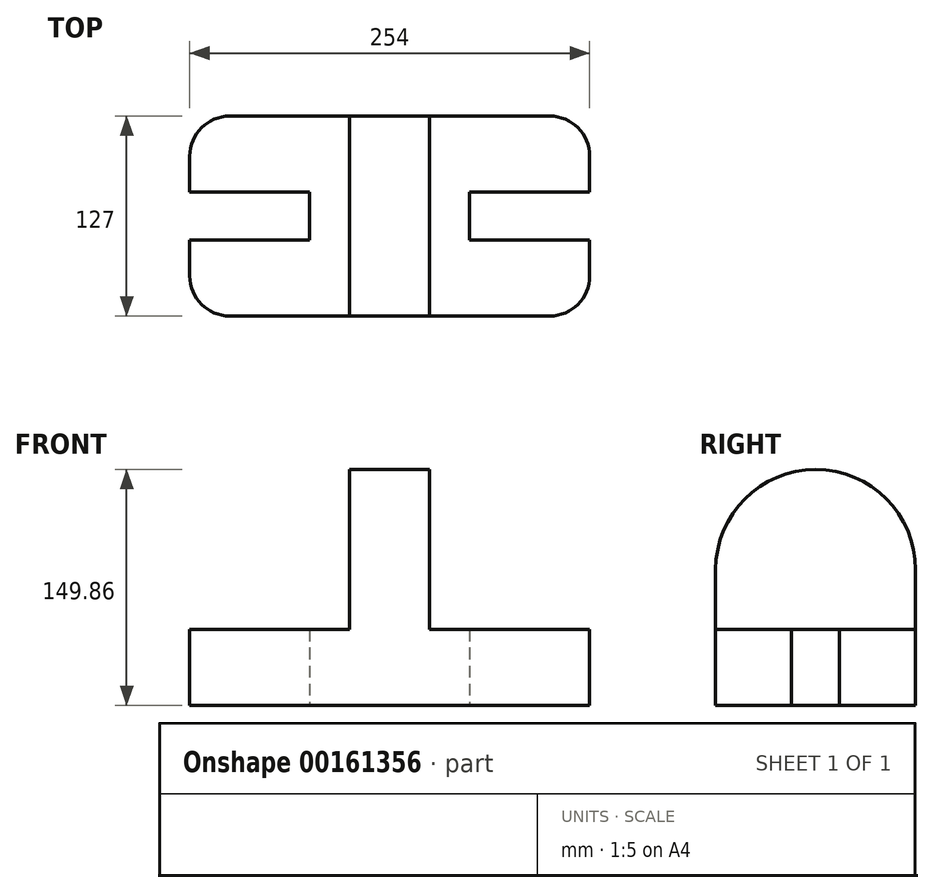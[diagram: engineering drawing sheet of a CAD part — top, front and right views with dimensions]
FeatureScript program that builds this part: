
annotation { "Feature Type Name" : "Feature", "Feature Type Description" : "" }
export const myFeature = defineFeature(function(context is Context, id is Id, definition is map)
    precondition{}
    {
        {
            var Q0;
            Q0=qCreatedBy(makeId("Top.planeOp"),FACE);
            var sketch = newSketch(context, id + "F0", { "sketchPlane" : qUnion([Q0])});
            skLineSegment(sketch, "E0", {"start": v(0, 0) * mm, "end": v(0, 48.26) * mm});
            skLineSegment(sketch, "E1", {"start": v(0, 48.26) * mm, "end": v(-76.2, 48.26) * mm});
            skLineSegment(sketch, "E2", {"start": v(-76.2, 48.26) * mm, "end": v(-76.2, 78.74) * mm});
            skLineSegment(sketch, "E3", {"start": v(-76.2, 78.74) * mm, "end": v(0, 78.74) * mm});
            skLineSegment(sketch, "E4", {"start": v(0, 78.74) * mm, "end": v(0, 127) * mm});
            skLineSegment(sketch, "E5", {"start": v(0, 127) * mm, "end": v(-254, 127) * mm});
            skLineSegment(sketch, "E6", {"start": v(0, 0) * mm, "end": v(-254, 0) * mm});
            skLineSegment(sketch, "E7", {"start": v(-254, 127) * mm, "end": v(-254, 78.74) * mm});
            skLineSegment(sketch, "E8", {"start": v(-254, 0) * mm, "end": v(-254, 48.26) * mm});
            skLineSegment(sketch, "E9", {"start": v(-254, 48.26) * mm, "end": v(-177.8, 48.26) * mm});
            skLineSegment(sketch, "E10", {"start": v(-177.8, 48.26) * mm, "end": v(-177.8, 78.74) * mm});
            skLineSegment(sketch, "E11", {"start": v(-177.8, 78.74) * mm, "end": v(-254, 78.74) * mm});
            skLineSegment(sketch, "E12", {"start": v(-152.4, 127) * mm, "end": v(-101.6, 127) * mm});
            skSolve(sketch);
        }
        {
            var Q0;
            {var subQ1=sQuery(id+"F0.wireOp",EDGE,"E7");Q0=makeQuery(id+"F0.imprint","IMPRINT",FACE,{"disambiguationData":[TD([[makeQuery(id+"F0.imprint","IMPRINT",EDGE,{"derivedFrom":subQ1}),1.0]])]});}
            var Q1;
            {var subQ0=sQuery(id+"F0.wireOp",EDGE,"2u5OPpGf-hsZS-RswZ-xJ63-mRApOYJbijJj");Q1=makeQuery(id+"F0.imprint","IMPRINT",FACE,{"disambiguationData":[TD([[makeQuery(id+"F0.imprint","IMPRINT",EDGE,{"derivedFrom":subQ0}),1.0]])]});}
            var Q2;
            {var subQ0=sQuery(id+"F0.wireOp",EDGE,"E0");Q2=makeQuery(id+"F0.imprint","IMPRINT",FACE,{"disambiguationData":[TD([[makeQuery(id+"F0.imprint","IMPRINT",EDGE,{"derivedFrom":subQ0}),1.0]])]});}
            extrude(context, id + "F1", {"entities" : qUnion([Q0, Q1, Q2]), "depth" : 48.26 * mm});
        }
        {
            var Q0;
            Q0=makeQuery(id+"F1.opExtrude","CAP_FACE",FACE,{"disambiguationData":[OSD([sQuery(id+"F0.wireOp",EDGE,"E0"),sQuery(id+"F0.wireOp",EDGE,"E1"),sQuery(id+"F0.wireOp",EDGE,"E2"),sQuery(id+"F0.wireOp",EDGE,"E3"),sQuery(id+"F0.wireOp",EDGE,"E4"),sQuery(id+"F0.wireOp",EDGE,"E5"),sQuery(id+"F0.wireOp",EDGE,"E6"),sQuery(id+"F0.wireOp",EDGE,"E7"),sQuery(id+"F0.wireOp",EDGE,"E8"),sQuery(id+"F0.wireOp",EDGE,"E9"),sQuery(id+"F0.wireOp",EDGE,"E10"),sQuery(id+"F0.wireOp",EDGE,"E11"),sQuery(id+"F0.wireOp",EDGE,"E12")])],"isStart":false});
            var sketch = newSketch(context, id + "F2", { "sketchPlane" : qUnion([Q0])});
            skLineSegment(sketch, "E13", {"start": v(-127, 127) * mm, "end": v(-152.4, 127) * mm});
            skLineSegment(sketch, "E14", {"start": v(-127, 127) * mm, "end": v(-101.6, 127) * mm});
            skLineSegment(sketch, "E15", {"start": v(-152.4, 127) * mm, "end": v(-152.4, 0) * mm});
            skLineSegment(sketch, "E16", {"start": v(-101.6, 127) * mm, "end": v(-101.6, 0) * mm});
            skSolve(sketch);
        }
        {
            var Q0;
            Q0=makeQuery(id+"F2.imprint","IMPRINT",FACE,{"disambiguationData":[TD([[makeQuery(id+"F2.imprint","IMPRINT",EDGE,{"derivedFrom":sQuery(id+"F2.wireOp",EDGE,"E13")}),1.0]])]});
            extrude(context, id + "F3", {"entities" : qUnion([Q0]), "operationType" : NewBodyOperationType.ADD, "depth" : 101.6 * mm});
        }
        {
            var Q0;
            Q0=makeQuery(id+"F3.opExtrude","CAP_EDGE",EDGE,{"disambiguationData":[OSD([sQuery(id+"F0.wireOp",EDGE,"E6")])],"isStart":false});
            var Q1;
            Q1=makeQuery(id+"F3.opExtrude","CAP_EDGE",EDGE,{"disambiguationData":[OSD([sQuery(id+"F2.wireOp",EDGE,"E13"),sQuery(id+"F2.wireOp",EDGE,"E14")])],"isStart":false});
            fillet(context, id + "F4", {"entities" : qUnion([Q0, Q1]), "radius" : 63.5 * mm, "tangentPropagation" : true, "allowEdgeOverflow" : false});
        }
        {
            var Q0;
            Q0=makeQuery(id+"F1.opExtrude","SWEPT_EDGE",EDGE,{"disambiguationData":[OSD([sQuery(id+"F0.wireOp",EDGE,"E6"),sQuery(id+"F0.wireOp",EDGE,"E8")])]});
            var Q1;
            Q1=makeQuery(id+"F1.opExtrude","SWEPT_EDGE",EDGE,{"disambiguationData":[OSD([sQuery(id+"F0.wireOp",EDGE,"E0"),sQuery(id+"F0.wireOp",EDGE,"E6")])]});
            var Q2;
            Q2=makeQuery(id+"F1.opExtrude","SWEPT_EDGE",EDGE,{"disambiguationData":[OSD([sQuery(id+"F0.wireOp",EDGE,"E5"),sQuery(id+"F0.wireOp",EDGE,"E7")])]});
            var Q3;
            Q3=makeQuery(id+"F1.opExtrude","SWEPT_EDGE",EDGE,{"disambiguationData":[OSD([sQuery(id+"F0.wireOp",EDGE,"E4"),sQuery(id+"F0.wireOp",EDGE,"E5")])]});
            fillet(context, id + "F5", {"entities" : qUnion([Q0, Q1, Q2, Q3]), "radius" : 25.4 * mm, "tangentPropagation" : true, "allowEdgeOverflow" : false});
        }
    });
